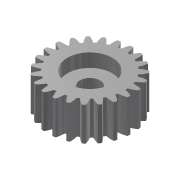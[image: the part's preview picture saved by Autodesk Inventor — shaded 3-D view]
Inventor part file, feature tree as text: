
AUTODESK INVENTOR PART (.ipt)
format: ipt  version: 2018 (Build 220112000, 112)  size: 260,608 bytes
history: native  units: mm (DEFAULTED — no unit token found)
features: sketch x5, extrude x4, plane x3, other x3
ambient origin geometry x8: Origin, YZ Plane, XZ Plane, XY Plane, X Axis, Y Axis, Z Axis, Center Point
bodies: Solid1 (feature_tree)
feature tree (15):
  extrude  "Extrusion1"  Depth=15.0mm TaperAngle=0.0deg
  plane  "Work Plane2"
  plane  "Work Plane8"
  plane  "Work Plane9"
  other  "正齒輪"
  extrude  "擠出7"  Depth=10.0mm TaperAngle=0.0deg
  extrude  "擠出8"  Depth=6.0mm
  extrude  "擠出9"  Depth=6.0mm TaperAngle=0.0deg
  sketch  "Sketch1"  dims[d0=37.5mm d1=15.0mm d2=0.0mm]
  sketch  "Sketch2"  dims[d3=34.5mm d4=10.0mm d5=0.0mm d16=60.0mm d17=0.0mm d34=1.36591mm d39=0.0mm d41=0.0mm d43=60.0mm d46=60.0mm d47=0.0mm d48=0.0mm d72=20.0mm d73=6.0mm d74=0.0mm d75=20.0mm d76=6.0mm d77=0.0mm d78=9.0mm d79=6.0mm d80=0.0mm]
  other  "Srf1"
  sketch  "草圖8"
  sketch  "草圖9"
  sketch  "草圖10"
  other  "節圓直徑"
